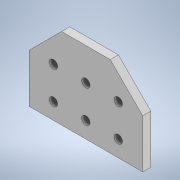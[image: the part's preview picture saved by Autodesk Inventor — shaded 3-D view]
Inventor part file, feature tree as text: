
AUTODESK INVENTOR PART (.ipt)
format: ipt  version: 2020 (Build 240168000, 168)  size: 120,320 bytes
history: native  units: in
note: dims shown in document units (in); Inventor stores cm internally (conversion verified against a paired STEP export)
features: extrude x1, sketch x1
ambient origin geometry x8: Origin, YZ Plane, XZ Plane, XY Plane, X Axis, Y Axis, Z Axis, Center Point
bodies: Solid1 (feature_tree)
feature tree (2):
  extrude  "Extrusion1"  Depth=1.0in
  sketch  "Sketch1"  dims[d5=2.5in d6=1.0in d7=1.5in d8=1.0in d9=1.0in d10=1.5in d11=1.0in d12=1.0in d13=1.5in d14=135.0deg d15=135.0deg d16=90.0deg d17=0.256in d18=0.5in d19=0.75in d20=0.7874in d22=1.0in d23=0.3937in d25=1.0in d27=1.1811in d29=1.0in d30=0.3937in d32=1.0in d34=0.25in d35=0.0in d36=0.5in d37=0.0344in]
